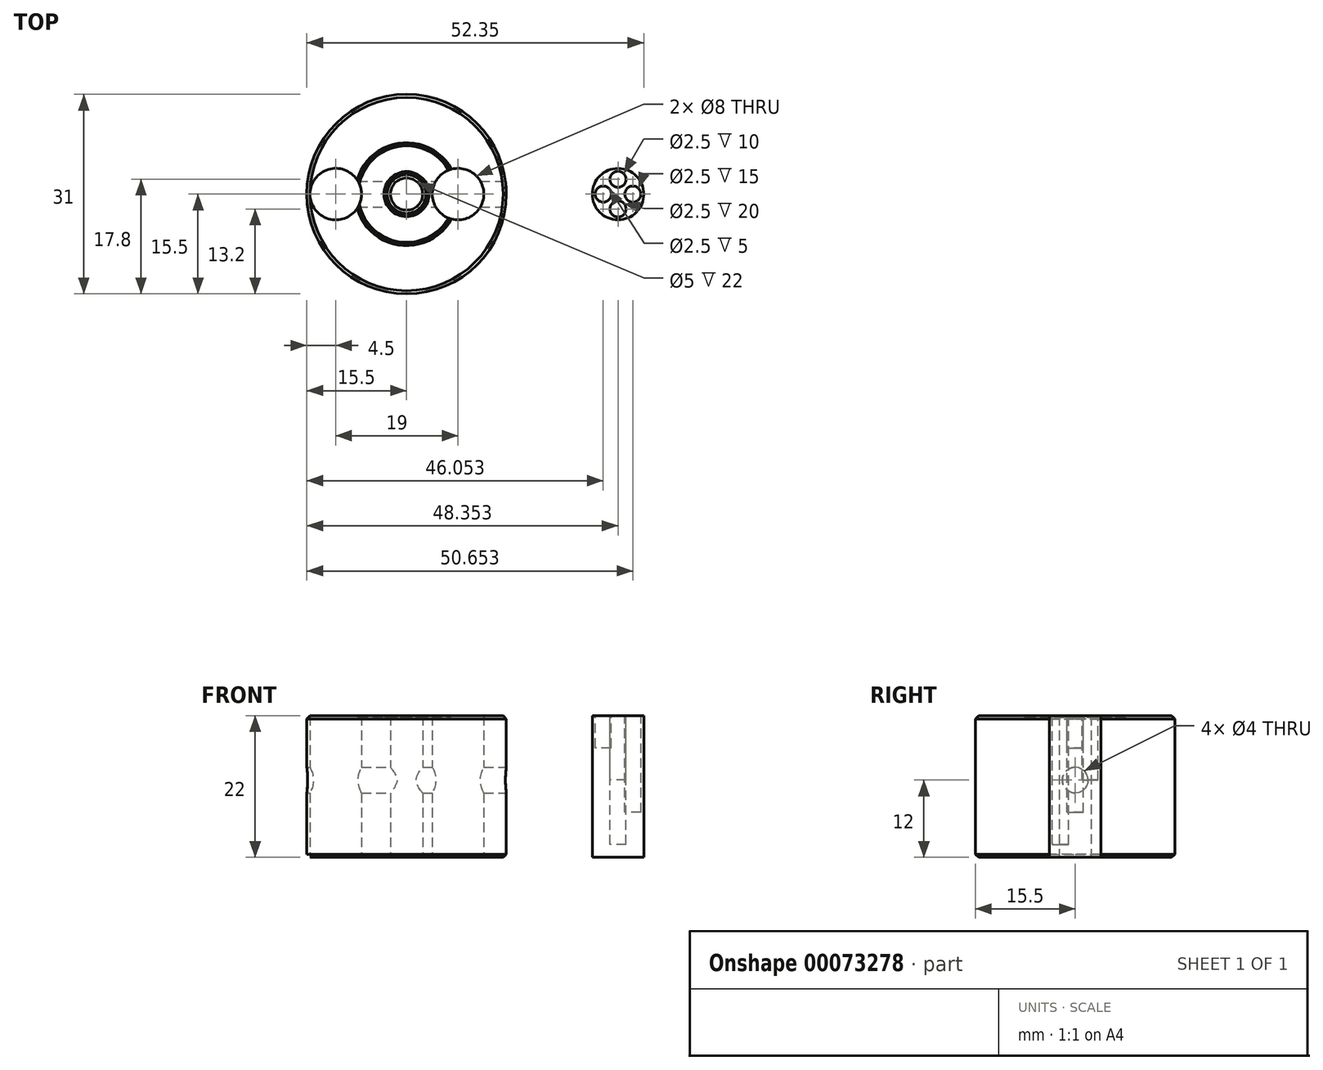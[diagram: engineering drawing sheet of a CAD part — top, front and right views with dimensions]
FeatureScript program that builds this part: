
annotation { "Feature Type Name" : "Feature", "Feature Type Description" : "" }
export const myFeature = defineFeature(function(context is Context, id is Id, definition is map)
    precondition{}
    {
        {
            var Q0;
            Q0=qCreatedBy(makeId("Top.planeOp"),FACE);
            var sketch = newSketch(context, id + "F0", { "sketchPlane" : qUnion([Q0])});
            skCircle(sketch, "E0", {"center": v(0, 0) * mm, "radius": 15.5 * mm});
            skCircle(sketch, "E1", {"center": v(0, 0) * mm, "radius": 2.5 * mm});
            skCircle(sketch, "E2", {"center": v(-11, 0) * mm, "radius": 4 * mm});
            skCircle(sketch, "E3", {"center": v(8, 0) * mm, "radius": 4 * mm});
            skSolve(sketch);
        }
        {
            var Q0;
            Q0 = qSketchRegion(id + "F0", true);
            extrude(context, id + "F1", {"entities" : qUnion([Q0]), "depth" : 22 * mm});
        }
        {
            var Q0;
            Q0=qCreatedBy(makeId("Right.planeOp"),FACE);
            var sketch = newSketch(context, id + "F2", { "sketchPlane" : qUnion([Q0])});
            skCircle(sketch, "E4", {"center": v(0, 12) * mm, "radius": 2 * mm});
            skSolve(sketch);
        }
        {
            var Q0;
            Q0=makeQuery(id+"F2.imprint","IMPRINT",FACE,{"disambiguationData":[TD([[makeQuery(id+"F2.imprint","IMPRINT",EDGE,{"derivedFrom":sQuery(id+"F2.wireOp",EDGE,"E4")}),1.0]])]});
            extrude(context, id + "F3", {"entities" : qUnion([Q0]), "operationType" : NewBodyOperationType.REMOVE, "endBound" : BoundingType.SYMMETRIC, "oppositeDirection" : true, "depth" : 32 * mm});
        }
        {
            var Q0;
            Q0=qCreatedBy(makeId("Top.planeOp"),FACE);
            var sketch = newSketch(context, id + "F4", { "sketchPlane" : qUnion([Q0])});
            skCircle(sketch, "E5", {"center": v(32.85, 0) * mm, "radius": 4 * mm});
            skSolve(sketch);
        }
        {
            var Q0;
            Q0 = qSketchRegion(id + "F4", true);
            extrude(context, id + "F5", {"entities" : qUnion([Q0]), "depth" : 22 * mm});
        }
        {
            var Q0;
            Q0=makeQuery(id+"F5.opExtrude","CAP_FACE",FACE,{"disambiguationData":[OSD([sQuery(id+"F4.wireOp",EDGE,"E5")])],"isStart":false});
            var sketch = newSketch(context, id + "F6", { "sketchPlane" : qUnion([Q0])});
            skCircle(sketch, "E6", {"center": v(35.15, 0) * mm, "radius": 1.25 * mm});
            skCircle(sketch, "E7.1.0", {"center": v(32.85, 2.3) * mm, "radius": 1.25 * mm});
            skCircle(sketch, "E7.2.0", {"center": v(30.55, 0) * mm, "radius": 1.25 * mm});
            skPoint(sketch, "E7.center", {"position": v(32.85, 0) * mm});
            skCircle(sketch, "E8.1.3.0", {"center": v(32.85, -2.3) * mm, "radius": 1.25 * mm});
            skSolve(sketch);
        }
        {
            var Q0;
            Q0=makeQuery(id+"F6.imprint","IMPRINT",FACE,{"disambiguationData":[TD([[makeQuery(id+"F6.imprint","IMPRINT",EDGE,{"derivedFrom":sQuery(id+"F6.wireOp",EDGE,"E7.1.0")}),1.0]])]});
            extrude(context, id + "F7", {"entities" : qUnion([Q0]), "operationType" : NewBodyOperationType.REMOVE, "oppositeDirection" : true, "depth" : 10 * mm});
        }
        {
            var Q0;
            Q0=makeQuery(id+"F6.imprint","IMPRINT",FACE,{"disambiguationData":[TD([[makeQuery(id+"F6.imprint","IMPRINT",EDGE,{"derivedFrom":sQuery(id+"F6.wireOp",EDGE,"E6")}),1.0]])]});
            extrude(context, id + "F8", {"entities" : qUnion([Q0]), "operationType" : NewBodyOperationType.REMOVE, "oppositeDirection" : true, "depth" : 15 * mm});
        }
        {
            var Q0;
            Q0=makeQuery(id+"F6.imprint","IMPRINT",FACE,{"disambiguationData":[TD([[makeQuery(id+"F6.imprint","IMPRINT",EDGE,{"derivedFrom":sQuery(id+"F6.wireOp",EDGE,"E8.1.3.0")}),1.0]])]});
            extrude(context, id + "F9", {"entities" : qUnion([Q0]), "operationType" : NewBodyOperationType.REMOVE, "oppositeDirection" : true, "depth" : 20 * mm});
        }
        {
            var Q0;
            Q0=makeQuery(id+"F6.imprint","IMPRINT",FACE,{"disambiguationData":[TD([[makeQuery(id+"F6.imprint","IMPRINT",EDGE,{"derivedFrom":sQuery(id+"F6.wireOp",EDGE,"E7.2.0")}),1.0]])]});
            extrude(context, id + "F10", {"entities" : qUnion([Q0]), "operationType" : NewBodyOperationType.REMOVE, "oppositeDirection" : true, "depth" : 5 * mm});
        }
        {
            var Q0;
            Q0=makeQuery(id+"F1.opExtrude","CAP_EDGE",EDGE,{"disambiguationData":[OSD([sQuery(id+"F0.wireOp",EDGE,"E0")])],"isStart":false});
            chamfer(context, id + "F11", {"entities" : qUnion([Q0]), "width" : 0.5 * mm, "tangentPropagation" : true});
        }
        {
            var Q0;
            Q0=makeQuery(id+"F1.opExtrude","CAP_EDGE",EDGE,{"disambiguationData":[OSD([sQuery(id+"F0.wireOp",EDGE,"E0")])],"isStart":true});
            chamfer(context, id + "F12", {"entities" : qUnion([Q0]), "width" : 0.5 * mm, "tangentPropagation" : true});
        }
        {
            var Q0;
            Q0=qCreatedBy(makeId("Front.planeOp"),FACE);
            var sketch = newSketch(context, id + "F13", { "sketchPlane" : qUnion([Q0])});
            skLineSegment(sketch, "E9", {"start": v(3, 22) * mm, "end": v(3.25, 21.75) * mm});
            skLineSegment(sketch, "E10", {"start": v(3.25, 21.75) * mm, "end": v(3.5, 22) * mm});
            skLineSegment(sketch, "E11", {"start": v(3, 22) * mm, "end": v(3.5, 22) * mm});
            skLineSegment(sketch, "E12", {"start": v(0, 22) * mm, "end": v(0, 12.97) * mm, "construction": true});
            skLineSegment(sketch, "E13", {"start": v(7.5, 22) * mm, "end": v(8, 22) * mm});
            skLineSegment(sketch, "E14", {"start": v(7.5, 22) * mm, "end": v(7.75, 21.74) * mm});
            skLineSegment(sketch, "E15", {"start": v(7.75, 21.74) * mm, "end": v(8, 22) * mm});
            skSolve(sketch);
        }
        {
            var Q0;
            Q0=makeQuery(id+"F13.imprint","IMPRINT",FACE,{"disambiguationData":[TD([[makeQuery(id+"F13.imprint","IMPRINT",EDGE,{"derivedFrom":sQuery(id+"F13.wireOp",EDGE,"E9")}),1.0]])]});
            var Q1;
            Q1=makeQuery(id+"F13.imprint","IMPRINT",FACE,{"disambiguationData":[TD([[makeQuery(id+"F13.imprint","IMPRINT",EDGE,{"derivedFrom":sQuery(id+"F13.wireOp",EDGE,"E13")}),-1.0]])]});
            var Q2;
            Q2=sQuery(id+"F13.wireOp",EDGE,"E12");
            revolve(context, id + "F14", {"operationType" : NewBodyOperationType.REMOVE, "entities" : qUnion([Q0, Q1]), "axis" : qUnion([Q2]), "revolveType" : RevolveType.FULL, "oppositeDirection" : true});
        }
    });
